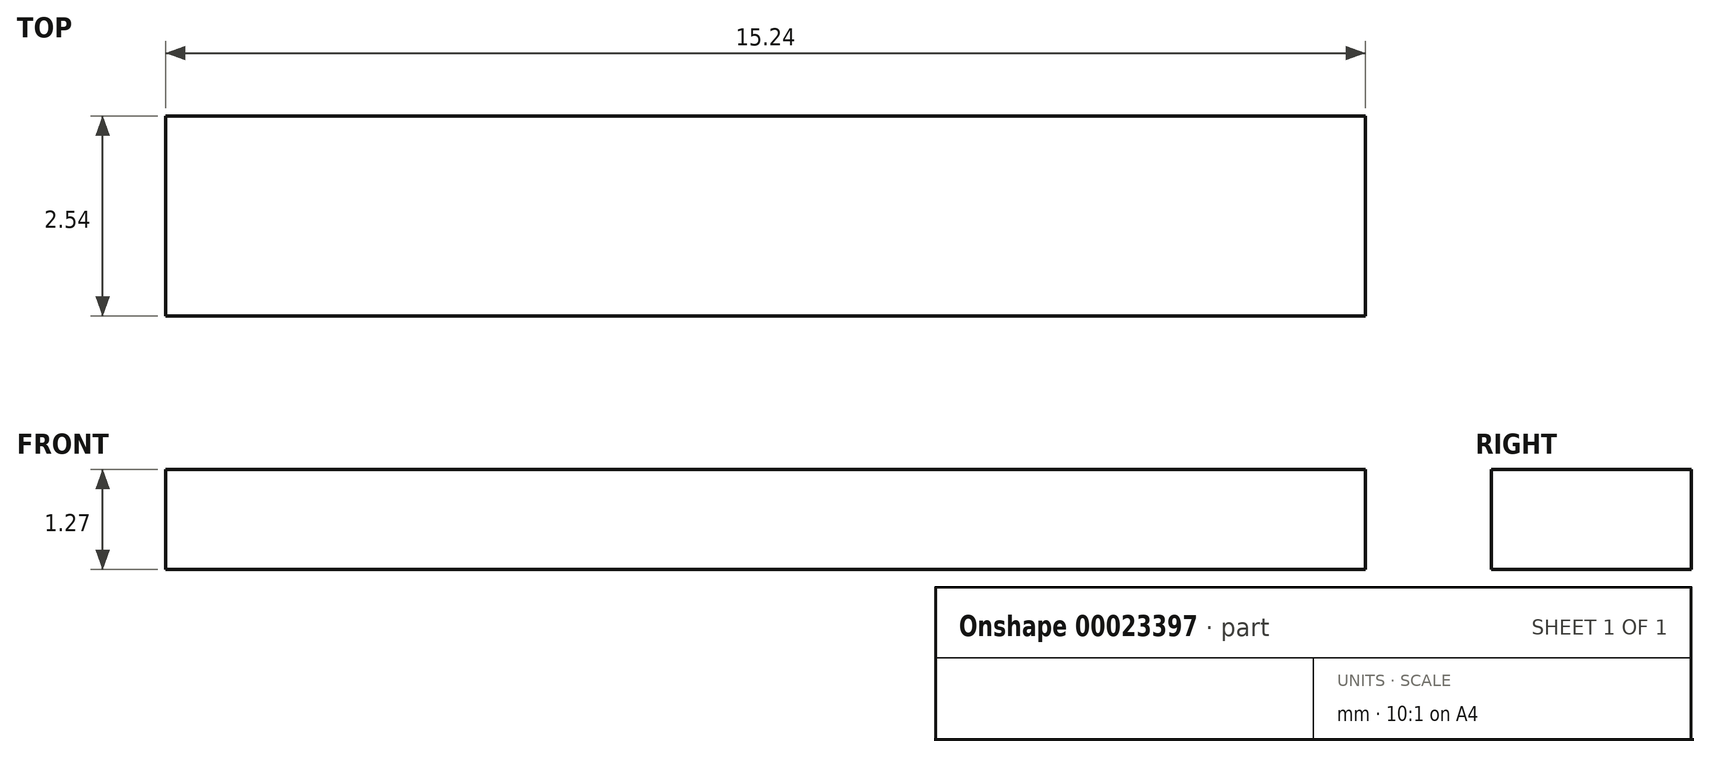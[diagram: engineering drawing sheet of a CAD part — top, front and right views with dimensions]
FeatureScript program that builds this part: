
annotation { "Feature Type Name" : "Feature", "Feature Type Description" : "" }
export const myFeature = defineFeature(function(context is Context, id is Id, definition is map)
    precondition{}
    {
        {
            var Q0;
            Q0=qCreatedBy(makeId("Front.planeOp"),FACE);
            var sketch = newSketch(context, id + "F0", { "sketchPlane" : qUnion([Q0])});
            skLineSegment(sketch, "E0.bottom", {"start": v(0, 0) * mm, "end": v(-15.24, 0) * mm});
            skLineSegment(sketch, "E0.top", {"start": v(0, 1.27) * mm, "end": v(-15.24, 1.27) * mm});
            skLineSegment(sketch, "E0.left", {"start": v(0, 0) * mm, "end": v(0, 1.27) * mm});
            skLineSegment(sketch, "E0.right", {"start": v(-15.24, 0) * mm, "end": v(-15.24, 1.27) * mm});
            skSolve(sketch);
        }
        {
            var Q0;
            Q0=makeQuery(id+"F0.imprint","IMPRINT",FACE,{"disambiguationData":[TD([[makeQuery(id+"F0.imprint","IMPRINT",EDGE,{"derivedFrom":sQuery(id+"F0.wireOp",EDGE,"E0.bottom")}),-1.0]])]});
            extrude(context, id + "F1", {"entities" : qUnion([Q0]), "depth" : 2.54 * mm});
        }
    });
